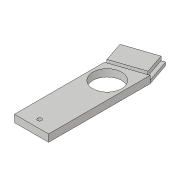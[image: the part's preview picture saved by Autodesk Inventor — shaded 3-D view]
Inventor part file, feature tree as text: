
AUTODESK INVENTOR PART (.ipt)
format: ipt  version: 2018.3 (Build 223284000, 284)  size: 120,320 bytes
history: native  units: in
note: dims shown in document units (in); Inventor stores cm internally (conversion verified against a paired STEP export)
features: extrude x4, sketch x4
ambient origin geometry x8: Origin, YZ Plane, XZ Plane, XY Plane, X Axis, Y Axis, Z Axis, Center Point
bodies: Solid1 (feature_tree)
feature tree (8):
  extrude  "Extrusion1"  Depth=0.119in
  extrude  "Extrusion2"  Depth=0.1105in
  extrude  "Extrusion3"  Depth=0.125in
  extrude  "Extrusion4"  Depth=1.0429in
  sketch  "Sketch1"  dims[d2=1.1in d4=0.88in d5=0.221in d6=0.0in d11=0.119in]
  sketch  "Sketch2"  dims[d13=0.125in d14=0.0in d17=0.1105in]
  sketch  "Sketch3"  dims[d18=0.125in d19=0.0in d24=0.75in]
  sketch  "Sketch4"  dims[d25=2.75in d26=0.75in d28=1.0429in d29=0.5215in d30=0.126in d31=0.5215in d32=0.25in d33=1.0in d34=0.0in d35=2.3125in]
